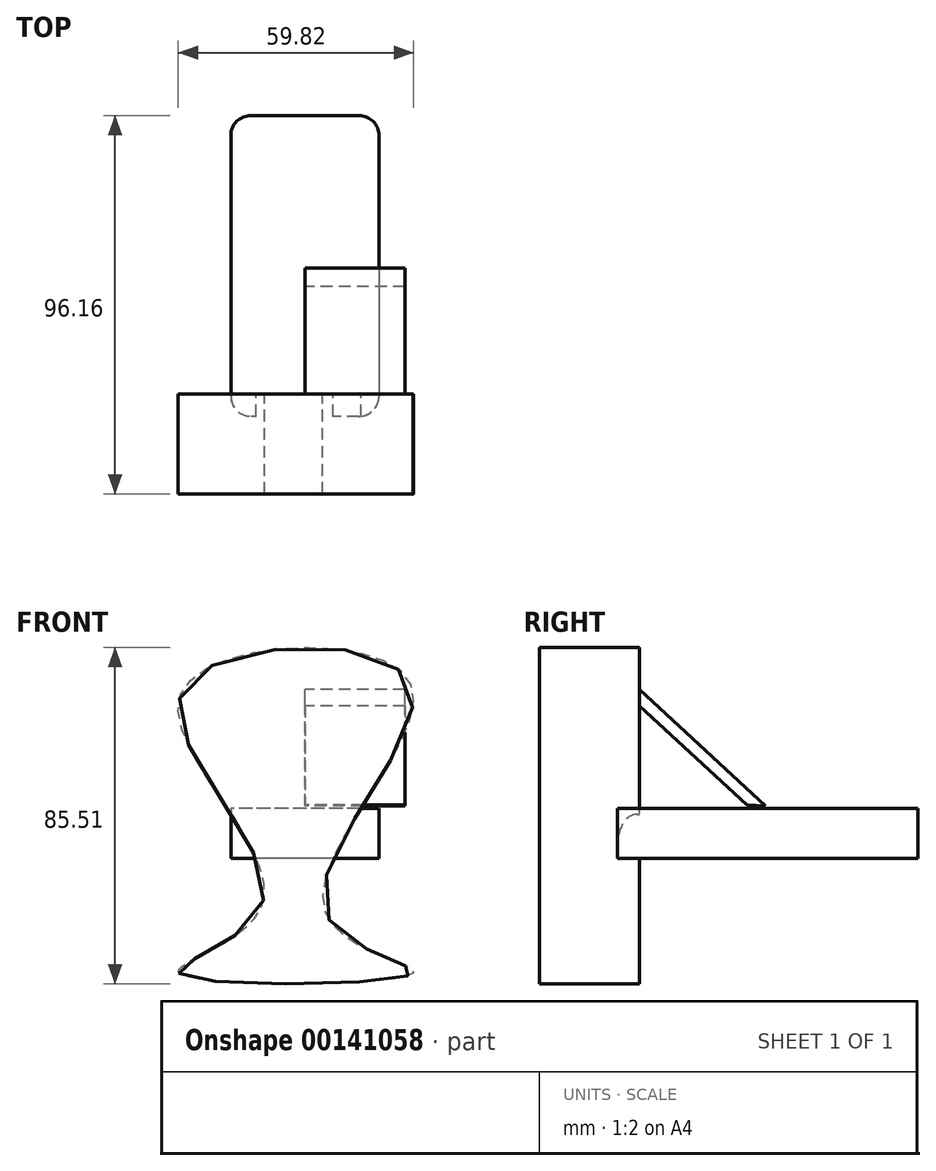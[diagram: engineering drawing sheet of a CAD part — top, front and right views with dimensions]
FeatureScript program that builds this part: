
annotation { "Feature Type Name" : "Feature", "Feature Type Description" : "" }
export const myFeature = defineFeature(function(context is Context, id is Id, definition is map)
    precondition{}
    {
        {
            var Q0;
            Q0=qCreatedBy(makeId("Front.planeOp"),FACE);
            var sketch = newSketch(context, id + "F0", { "sketchPlane" : qUnion([Q0])});
            skFitSpline(sketch, "E0", {"points": [v(-31.94, -29.13) * mm, v(-10.75, -11.4) * mm, v(-31.35, 42.22) * mm, v(26.57, 44.75) * mm, v(5.08, -13.51) * mm, v(27.47, -29.13) * mm, v(-31.94, -29.13) * mm]});
            skSolve(sketch);
        }
        {
            var Q0;
            Q0=makeQuery(id+"F0.imprint","IMPRINT",FACE,{"disambiguationData":[TD([[makeQuery(id+"F0.imprint","IMPRINT",EDGE,{"derivedFrom":sQuery(id+"F0.wireOp",EDGE,"E0")}),-1.0]])]});
            extrude(context, id + "F1", {"entities" : qUnion([Q0]), "depth" : 25.4 * mm});
        }
        {
            var Q0;
            Q0=qCreatedBy(makeId("Top.planeOp"),FACE);
            var sketch = newSketch(context, id + "F2", { "sketchPlane" : qUnion([Q0])});
            skLineSegment(sketch, "E1.bottom", {"start": v(13.73, 70.76) * mm, "end": v(-13.73, 70.76) * mm});
            skLineSegment(sketch, "E1.top", {"start": v(13.73, -5.67) * mm, "end": v(-13.73, -5.67) * mm});
            skLineSegment(sketch, "E1.left", {"start": v(18.8, 65.68) * mm, "end": v(18.8, -0.6) * mm});
            skLineSegment(sketch, "E1.right", {"start": v(-18.8, 65.68) * mm, "end": v(-18.8, -0.6) * mm});
            skPoint(sketch, "E1.middle", {"position": v(0, 32.54) * mm});
            skPoint(sketch, "E2.visualSharp", {"position": v(-18.8, 70.76) * mm});
            skArc(sketch, "E2.filletArc", {"start": v(-13.73, 70.76) * mm, "mid": v(-17.32, 69.27) * mm, "end": v(-18.8, 65.68) * mm});
            skPoint(sketch, "E3.visualSharp", {"position": v(18.8, 70.76) * mm});
            skArc(sketch, "E3.filletArc", {"start": v(18.8, 65.68) * mm, "mid": v(17.32, 69.27) * mm, "end": v(13.73, 70.76) * mm});
            skPoint(sketch, "E4.visualSharp", {"position": v(18.8, -5.67) * mm});
            skArc(sketch, "E4.filletArc", {"start": v(13.73, -5.67) * mm, "mid": v(17.32, -4.18) * mm, "end": v(18.8, -0.6) * mm});
            skPoint(sketch, "E5.visualSharp", {"position": v(-18.8, -5.67) * mm});
            skArc(sketch, "E5.filletArc", {"start": v(-18.8, -0.6) * mm, "mid": v(-17.32, -4.18) * mm, "end": v(-13.73, -5.67) * mm});
            skSolve(sketch);
        }
        {
            var Q0;
            Q0 = qSketchRegion(id + "F2", true);
            extrude(context, id + "F3", {"entities" : qUnion([Q0]), "operationType" : NewBodyOperationType.ADD, "depth" : 12.7 * mm});
        }
        {
            var Q0;
            Q0=qCreatedBy(makeId("Right.planeOp"),FACE);
            var sketch = newSketch(context, id + "F4", { "sketchPlane" : qUnion([Q0])});
            skLineSegment(sketch, "E6", {"start": v(31.94, 13.43) * mm, "end": v(0, 43) * mm});
            skLineSegment(sketch, "E7", {"start": v(0, 38.81) * mm, "end": v(27.26, 13.59) * mm});
            skLineSegment(sketch, "E8", {"start": v(0, 38.81) * mm, "end": v(0, 43) * mm});
            skLineSegment(sketch, "E9", {"start": v(27.26, 13.59) * mm, "end": v(31.94, 13.43) * mm});
            skSolve(sketch);
        }
        {
            var Q0;
            Q0 = qSketchRegion(id + "F4", true);
            extrude(context, id + "F5", {"entities" : qUnion([Q0]), "operationType" : NewBodyOperationType.ADD, "depth" : 25.4 * mm});
        }
    });
